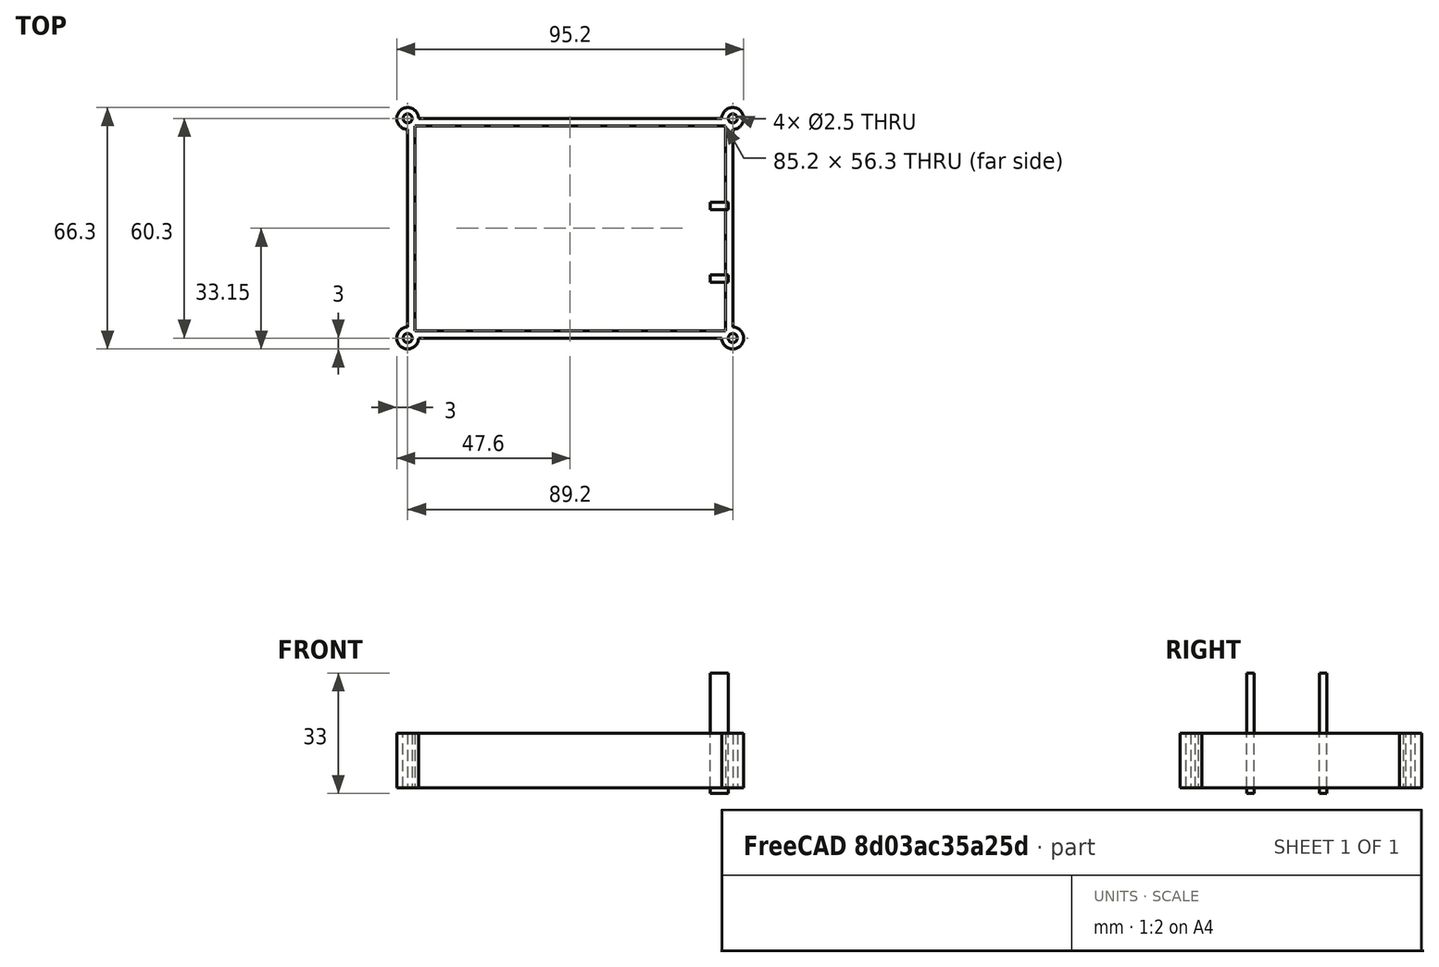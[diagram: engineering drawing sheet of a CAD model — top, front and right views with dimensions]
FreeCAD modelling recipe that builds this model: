
FCSTD DOCUMENT  (FreeCAD 0.18.4R)
Label: OrangePI_PC_Case
License: All rights reserved
LicenseURL: http://en.wikipedia.org/wiki/All_rights_reserved
objects: Part::Feature×5, Mesh::Feature×4, App::Part×2, Part::Plane×2, Part::Box×2, Sketcher::SketchObject×1, PartDesign::Pad×1, Part::Compound×1
note: 13 computed .brp shape members not serialized (recipe doc carries the construction recipe); baked Part::Feature solids carry a one-line shape summary decoded from their .brp

FEATURE [Part::Feature] OrangePI_PC_case___Top_with_GPIO_breakable_cover_by_MEXUS001001  label="OrangePI_PC_case___Top_with_GPIO_breakable_cover_by_MEXUS002"
  shape: bbox 95.28 x 66.29 x 20 mm, 4092 faces, 0 solids (baked)
FEATURE [App::Part] Part  label="top"
  Group = -> [OrangePI_PC_case___Top_with_GPIO_breakable_cover_by_MEXUS001001]
  Origin = -> Origin
FEATURE [Part::Plane] Plane
  AttacherType = Attacher::AttachEngine3D
  Length = 100
  Placement = pos=(-3,-20,0) rot=(0,0,1;0rad)
  Width = 100
FEATURE [Part::Plane] Plane001
  AttacherType = Attacher::AttachEngine3D
  Length = 100
  Placement = pos=(-3,-20,2.4) rot=(0,0,1;0rad)
  Width = 100
FEATURE [Mesh::Feature] OrangePI_PC_case___Top_with_GPIO_breakable_cover_by_MEXUS001003  label="OrangePI_PC_case_-_Top_with_GPIO_breakable_cover_by_MEXUS001"
  Placement = pos=(0,0,-64) rot=(0,0,1;0rad)
FEATURE [Sketcher::SketchObject] Sketch007
  Placement = pos=(0,0,3.5) rot=(0,0,1;0rad)
  sketch-geometry (17):
    g0: LineSegment StartX=89.2 StartY=63.3 StartZ=0 EndX=6 EndY=63.3 EndZ=0
    g1: LineSegment StartX=3 StartY=60.3 StartZ=0 EndX=3 EndY=6 EndZ=0
    g2: LineSegment StartX=5 StartY=61.3 StartZ=0 EndX=90.2 EndY=61.3 EndZ=0
    g3: LineSegment StartX=5 StartY=61.3 StartZ=0 EndX=5 EndY=5 EndZ=0
    g4: GeomPoint X=5 Y=5 Z=0
    g5: LineSegment StartX=5 StartY=5 StartZ=0 EndX=90.2 EndY=5 EndZ=0
    g6: LineSegment StartX=90.2 StartY=61.3 StartZ=0 EndX=90.2 EndY=5 EndZ=0
    g7: LineSegment StartX=92.2 StartY=60.3 StartZ=0 EndX=92.2 EndY=6 EndZ=0
    g8: LineSegment StartX=6 StartY=3 StartZ=0 EndX=89.2 EndY=3 EndZ=0
    g9: Circle CenterX=3 CenterY=63.3 CenterZ=0 NormalX=0 NormalY=0 NormalZ=1 AngleXU=0 Radius=1.25
    g10: Circle CenterX=92.2 CenterY=63.3 CenterZ=0 NormalX=0 NormalY=0 NormalZ=1 AngleXU=0 Radius=1.25
    g11: ArcOfCircle CenterX=3 CenterY=63.3 CenterZ=0 NormalX=0 NormalY=0 NormalZ=1 AngleXU=0 Radius=3 StartAngle=4.48068e-08 EndAngle=4.71239
    g12: Circle CenterX=3 CenterY=3 CenterZ=0 NormalX=0 NormalY=0 NormalZ=1 AngleXU=0 Radius=1.25
    g13: ArcOfCircle CenterX=3 CenterY=3 CenterZ=0 NormalX=0 NormalY=0 NormalZ=1 AngleXU=0 Radius=3 StartAngle=1.5708 EndAngle=6.28319
    g14: ArcOfCircle CenterX=92.2 CenterY=63.3 CenterZ=0 NormalX=0 NormalY=0 NormalZ=1 AngleXU=0 Radius=3 StartAngle=4.71239 EndAngle=9.42478
    g15: Circle CenterX=92.2 CenterY=3 CenterZ=0 NormalX=0 NormalY=0 NormalZ=1 AngleXU=0 Radius=1.25
    g16: ArcOfCircle CenterX=92.2 CenterY=3 CenterZ=0 NormalX=0 NormalY=0 NormalZ=1 AngleXU=0 Radius=3 StartAngle=3.14159 EndAngle=7.85398
  constraints (52):
    c: Horizontal(g0)
    c: Vertical(g1)
    c: Horizontal(g2)
    c: Vertical(g3)
    c: Vertical(g6)
    c: Equal(g6,g3)
    c: Vertical(g7)
    c: Equal(g7,g1)
    c: Horizontal(g8)
    c: Equal(g8,g0)
    c: Radius(g9) = 1.25
    c: Equal(g9,g10) = 1.25
    c: Coincident(g11,g9)
    c: Coincident(g0,g11)
    c: DistanceY(g9,g10) = 0
    c: Equal(g9,g12) = 1.25
    c: DistanceX(g9,g12) = 0
    c: Coincident(g13,g12)
    c: Coincident(g1,g13)
    c: Coincident(g14,g10)
    c: Coincident(g0,g14)
    c: Coincident(g7,g14)
    c: Equal(g0,g8)
    c: Equal(g6,g3)
    c: Equal(g1,g7)
    c: Coincident(g16,g15)
    c: Coincident(g6,g2)
    c: Coincident(g3,g2)
    c: Coincident(g3,g4)
    c: Coincident(g5,g3)
    c: Coincident(g5,g6)
    c: Coincident(g7,g16)
    c: Coincident(g8,g16)
    c: Coincident(g8,g13)
    c: DistanceY(g8,g3) = 2
    c: DistanceX(g3,g8) = 1
    c: DistanceX(g-1,g12) = 3
    c: DistanceY(g-1,g12) = 3
    c: DistanceX(g-1,g8) = 6
    c: DistanceY(g-1,g8) = 3
    c: DistanceY(g1,g7) = 0
    c: Coincident(g1,g11)
    c: DistanceY(g2,g0) = 2
    c: DistanceX(g2,g0) = 1
    c: DistanceX(g1,g3) = 2
    c: DistanceX(g2,g7) = 2
    c: DistanceY(g15,g12) = 0
    c: Equal(g16,g14)
    c: Equal(g14,g11)
    c: Equal(g15,g10)
    c: DistanceX(g5,g5) = 85.2
    c: DistanceY(g6,g6) = 56.3
FEATURE [Mesh::Feature] OrangePI_PC_case___Top_with_GPIO_breakable_cover_by_MEXUS001001002  label="OrangePI_PC_case_-_Top_with_GPIO_breakable_cover_by_MEXUS002"
FEATURE [Part::Feature] OrangePI_PC_case___Top_with_GPIO_breakable_cover_by_MEXUS001001002001
  shape: bbox 95.82 x 66.83 x 17.34 mm, 8060 faces, 0 solids (baked)
FEATURE [Part::Feature] OrangePI_PC_case___Top_with_GPIO_breakable_cover_by_MEXUS001001002001_solid  label="OrangePI_PC_case___Top_with_GPIO_breakable_cover_by_MEXUS001001002001 (Solid)"
  shape: bbox 95.82 x 66.83 x 17.34 mm, 8060 faces (baked)
FEATURE [Part::Feature] OrangePI_PC_case___Top_with_GPIO_breakable_cover_by_MEXUS001001002001_solid001  label="OrangePI_PC_case___Top_with_GPIO_breakable_cover_by_MEXUS001001002001 (Solid)001"
  shape: bbox 95.82 x 66.83 x 17.34 mm, 3441 faces (baked)
FEATURE [PartDesign::Pad] Pad
  Length = 15
  Length2 = 100
  Placement = pos=(0,0,3.5) rot=(0,0,1;0rad)
  Profile = -> Sketch007
  Refine = true
  Reversed = true
  Type = 0
FEATURE [Mesh::Feature] OrangePI_PC_case___Top_with_GPIO_breakable_cover_by_MEXUS001001002002  label="OrangePI_PC_case_-_Top_with_GPIO_breakable_cover_by_MEXUS003"
  Placement = pos=(0,0,-20) rot=(0,0,1;0rad)
FEATURE [Part::Feature] OrangePI_PC_case___Top_with_GPIO_breakable_cover_by_MEXUS001001002002001  label="top OrangePI_PC_case___Top_with_GPIO_breakable_cover_by_MEXUS001001002002001"
  Placement = pos=(0,0,6) rot=(0,0,1;0rad)
  shape: bbox 95.28 x 66.29 x 3.8 mm, 7773 faces, 0 solids (baked)
FEATURE [Part::Box] Box  label="Cube"
  AttacherType = Attacher::AttachEngine3D
  Height = 33
  Length = 5
  Placement = pos=(86,18.35,-13) rot=(0,0,1;0rad)
  Width = 2
FEATURE [Part::Box] Box003  label="Cube003"
  AttacherType = Attacher::AttachEngine3D
  Height = 33
  Length = 5
  Placement = pos=(86,38.25,-13) rot=(0,0,1;0rad)
  Width = 2
FEATURE [Part::Compound] Compound
  Links = -> [OrangePI_PC_case___Top_with_GPIO_breakable_cover_by_MEXUS001001002001_solid001,Pad,OrangePI_PC_case___Top_with_GPIO_breakable_cover_by_MEXUS001001002002001,Box,Box003]
FEATURE [App::Part] Part002  label="final box top part"
  Group = -> [OrangePI_PC_case___Top_with_GPIO_breakable_cover_by_MEXUS001001002002001,Sketch007,Pad,OrangePI_PC_case___Top_with_GPIO_breakable_cover_by_MEXUS001001002001_solid001,Compound,Box,Box003]
  Origin = -> Origin004
FEATURE [Mesh::Feature] OrangePI_PC_case___Bottom_with_wall_mount_holes_by_MEXUS  label="OrangePI_PC_case_-_Bottom_with_wall_mount_holes_by_MEXUS"
  Placement = pos=(0,74,-14) rot=(0,0,1;0rad)
